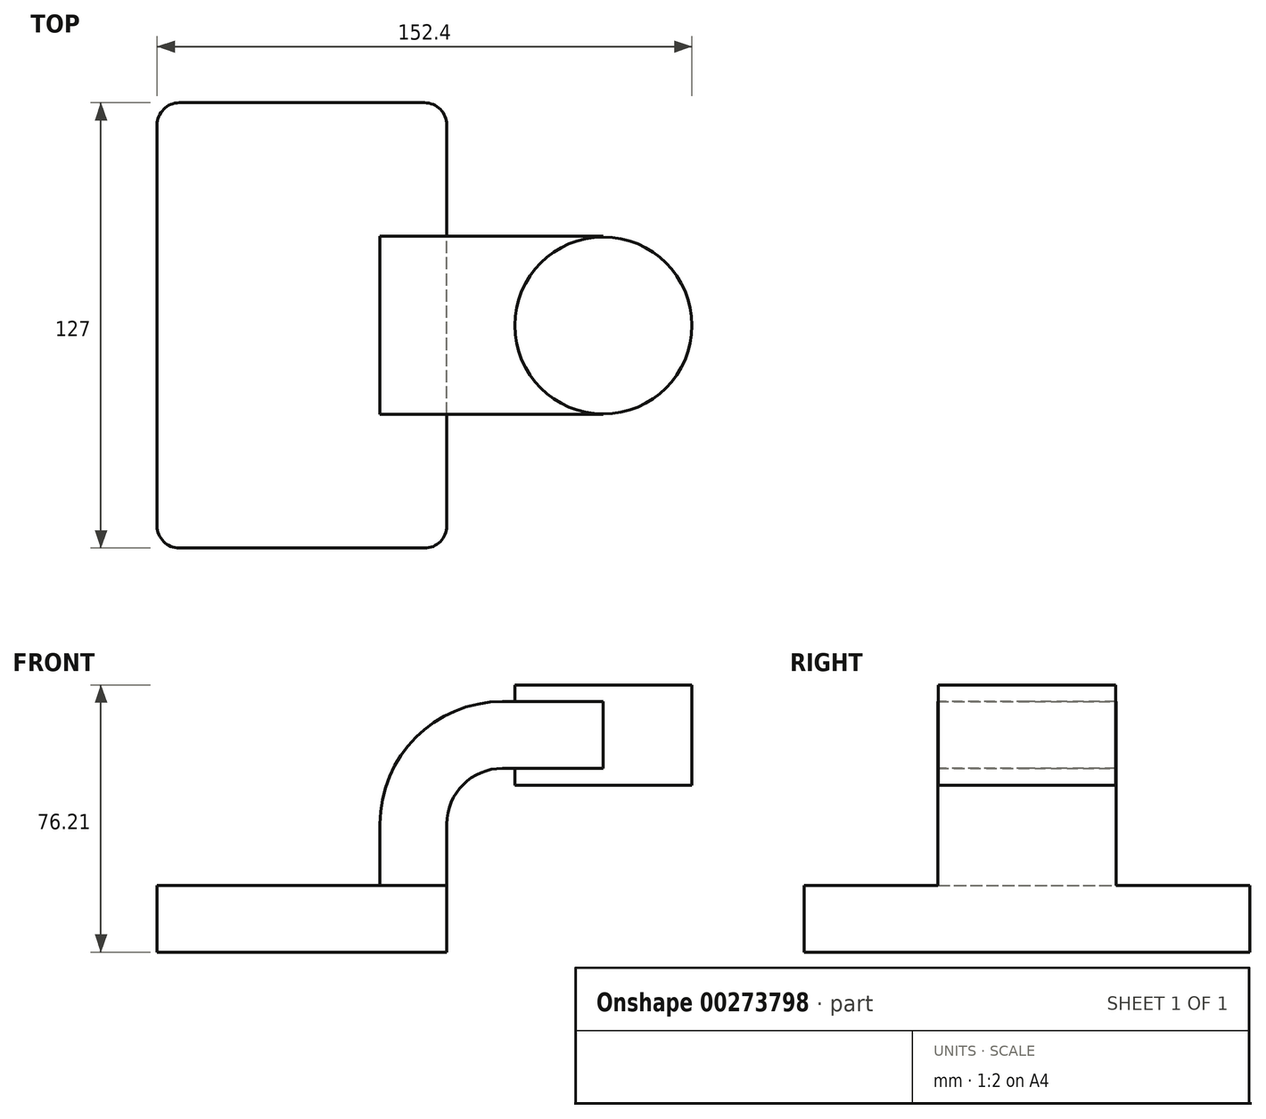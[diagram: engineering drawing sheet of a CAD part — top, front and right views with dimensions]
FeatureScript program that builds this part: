
annotation { "Feature Type Name" : "Feature", "Feature Type Description" : "" }
export const myFeature = defineFeature(function(context is Context, id is Id, definition is map)
    precondition{}
    {
        {
            var Q0;
            Q0=qCreatedBy(makeId("Front.planeOp"),FACE);
            var sketch = newSketch(context, id + "F0", { "sketchPlane" : qUnion([Q0])});
            skPoint(sketch, "E0.middle", {"position": v(0, 0) * mm});
            skLineSegment(sketch, "E1.bottom", {"start": v(41.28, -9.52) * mm, "end": v(-41.28, -9.53) * mm});
            skLineSegment(sketch, "E1.top", {"start": v(41.28, 9.53) * mm, "end": v(-41.28, 9.53) * mm});
            skLineSegment(sketch, "E1.left", {"start": v(41.28, -9.52) * mm, "end": v(41.28, 9.53) * mm});
            skLineSegment(sketch, "E1.right", {"start": v(-41.28, -9.52) * mm, "end": v(-41.28, 9.53) * mm});
            skLineSegment(sketch, "E2.bottom", {"start": v(60.32, 38.1) * mm, "end": v(111.12, 38.1) * mm});
            skLineSegment(sketch, "E2.top", {"start": v(60.32, 66.68) * mm, "end": v(111.12, 66.68) * mm});
            skLineSegment(sketch, "E2.left", {"start": v(60.32, 38.1) * mm, "end": v(60.32, 66.68) * mm});
            skLineSegment(sketch, "E2.right", {"start": v(111.12, 38.1) * mm, "end": v(111.12, 66.68) * mm});
            skPoint(sketch, "E2.middle", {"position": v(85.72, 52.39) * mm});
            skLineSegment(sketch, "E3", {"start": v(41.28, 9.53) * mm, "end": v(41.28, 27) * mm});
            skArc(sketch, "E4", {"start": v(41.27, 27) * mm, "mid": v(45.92, 38.23) * mm, "end": v(57.15, 42.88) * mm});
            skLineSegment(sketch, "E5", {"start": v(57.15, 42.88) * mm, "end": v(85.88, 42.88) * mm});
            skLineSegment(sketch, "E6.0", {"start": v(57.15, 61.93) * mm, "end": v(85.88, 61.93) * mm});
            skArc(sketch, "E6.1", {"start": v(22.23, 27) * mm, "mid": v(32.45, 51.7) * mm, "end": v(57.15, 61.93) * mm});
            skLineSegment(sketch, "E6.2", {"start": v(22.22, 9.53) * mm, "end": v(22.22, 27) * mm});
            skLineSegment(sketch, "E7", {"start": v(85.88, 38.1) * mm, "end": v(85.88, 66.68) * mm});
            skFitSpline(sketch, "E8", {"points": [v(-41.28, 9.53) * mm, v(57.15, 61.93) * mm], "startDerivative": vector(1.18, 149.12) * mm, "endDerivative": vector(122.08, -0.28) * mm});
            skSolve(sketch);
        }
        {
            var Q0;
            Q0=makeQuery(id+"F0.imprint","IMPRINT",FACE,{"disambiguationData":[TD([[makeQuery(id+"F0.imprint","IMPRINT",EDGE,{"derivedFrom":sQuery(id+"F0.wireOp",EDGE,"E1.bottom")}),-1.0]])]});
            extrude(context, id + "F1", {"entities" : qUnion([Q0]), "endBound" : BoundingType.SYMMETRIC, "depth" : 127 * mm});
        }
        {
            var Q0;
            {var subQ1=sQuery(id+"F0.wireOp",EDGE,"E3");Q0=makeQuery(id+"F0.imprint","IMPRINT",FACE,{"disambiguationData":[TD([[makeQuery(id+"F0.imprint","IMPRINT",EDGE,{"derivedFrom":subQ1}),1.0]])]});}
            var Q1;
            {var subQ0=sQuery(id+"F0.wireOp",EDGE,"E5");var subQ1=sQuery(id+"F0.wireOp",EDGE,"E2.left");var subQ2=makeQuery(id+"F0.imprint","INTERSECT",VERTEX,{"derivedFrom":[subQ1,subQ0]});Q1=makeQuery(id+"F0.imprint","IMPRINT",FACE,{"disambiguationData":[TD([[makeQuery(id+"F0.imprint","IMPRINT",EDGE,{"disambiguationData":[TD([[subQ2,-1.0]])],"derivedFrom":subQ1}),-1.0]])]});}
            extrude(context, id + "F2", {"entities" : qUnion([Q0, Q1]), "operationType" : NewBodyOperationType.ADD, "endBound" : BoundingType.SYMMETRIC, "depth" : 50.8 * mm});
        }
        {
            var Q0;
            Q0=makeQuery(id+"F0.imprint","IMPRINT",FACE,{"disambiguationData":[TD([[makeQuery(id+"F0.imprint","IMPRINT",EDGE,{"derivedFrom":sQuery(id+"F0.wireOp",EDGE,"E6.1")}),1.0]])]});
            extrude(context, id + "F3", {"entities" : qUnion([Q0]), "operationType" : NewBodyOperationType.ADD, "endBound" : BoundingType.SYMMETRIC, "depth" : 15.88 * mm});
        }
        {
            var Q0;
            {var subQ0=sQuery(id+"F0.wireOp",EDGE,"E2.right");Q0=makeQuery(id+"F0.imprint","IMPRINT",FACE,{"disambiguationData":[TD([[makeQuery(id+"F0.imprint","IMPRINT",EDGE,{"derivedFrom":subQ0}),1.0]])]});}
            var Q1;
            Q1=sQuery(id+"F0.wireOp",EDGE,"E7");
            revolve(context, id + "F4", {"operationType" : NewBodyOperationType.ADD, "entities" : qUnion([Q0]), "axis" : qUnion([Q1]), "revolveType" : RevolveType.FULL});
        }
        {
            var Q0;
            Q0=makeQuery(id+"F1.opExtrude","CAP_EDGE",EDGE,{"disambiguationData":[OSD([sQuery(id+"F0.wireOp",EDGE,"E1.right")])],"isStart":false});
            var Q1;
            Q1=makeQuery(id+"F1.opExtrude","CAP_EDGE",EDGE,{"disambiguationData":[OSD([sQuery(id+"F0.wireOp",EDGE,"E1.left")])],"isStart":false});
            var Q2;
            Q2=makeQuery(id+"F1.opExtrude","CAP_EDGE",EDGE,{"disambiguationData":[OSD([sQuery(id+"F0.wireOp",EDGE,"E1.left")])],"isStart":true});
            var Q3;
            Q3=makeQuery(id+"F1.opExtrude","CAP_EDGE",EDGE,{"disambiguationData":[OSD([sQuery(id+"F0.wireOp",EDGE,"E1.right")])],"isStart":true});
            fillet(context, id + "F5", {"entities" : qUnion([Q0, Q1, Q2, Q3]), "radius" : 6.35 * mm, "tangentPropagation" : true, "allowEdgeOverflow" : false});
        }
    });
